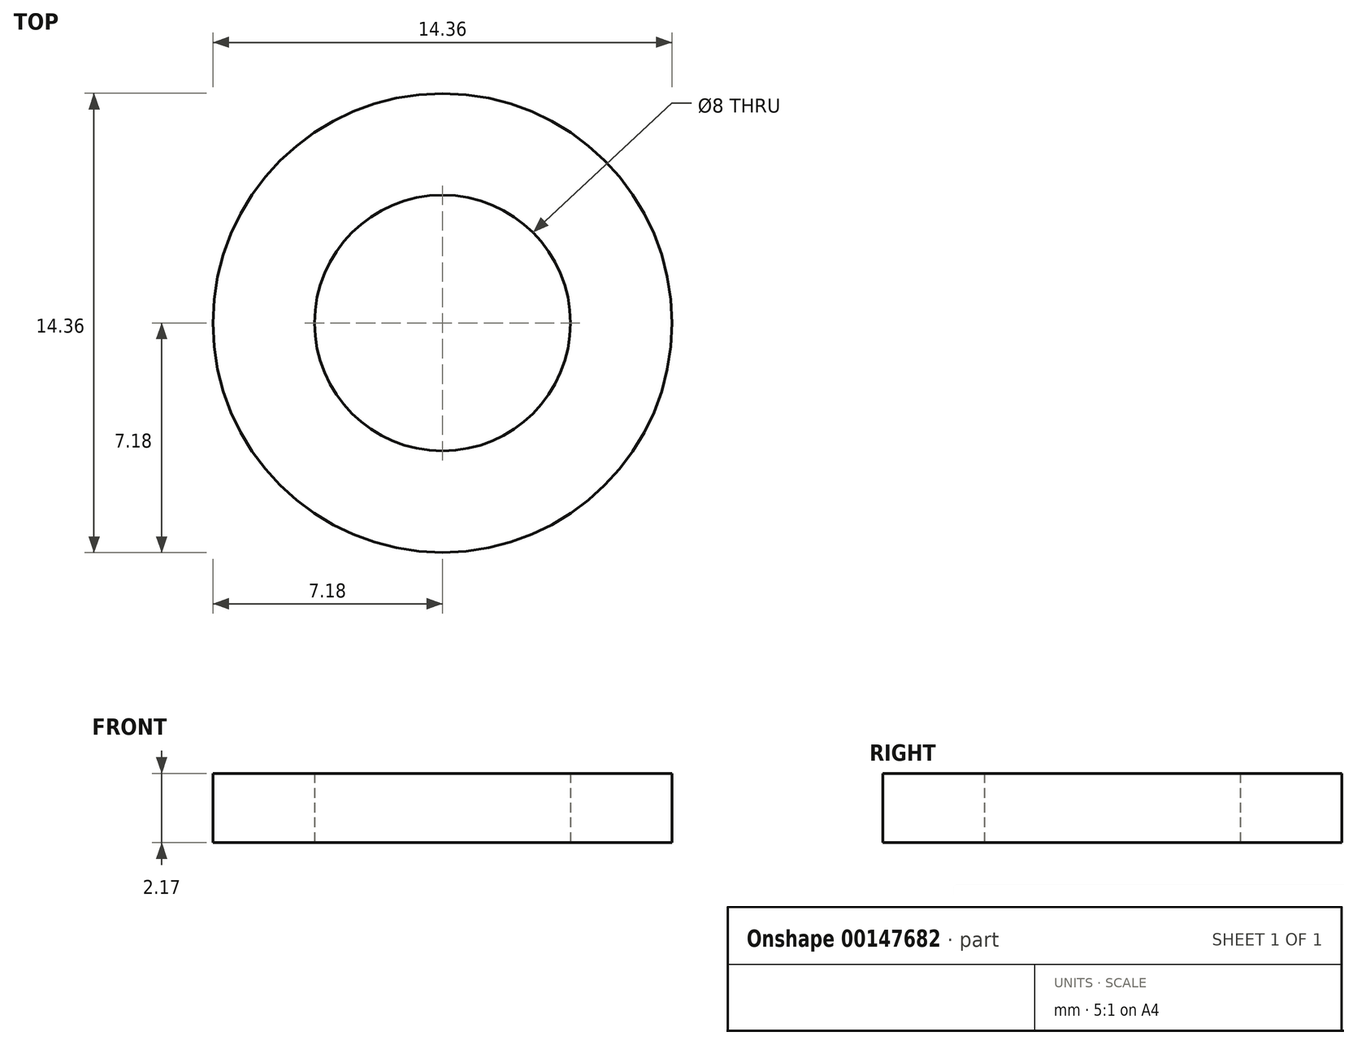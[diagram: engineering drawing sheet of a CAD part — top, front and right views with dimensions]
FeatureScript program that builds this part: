
annotation { "Feature Type Name" : "Feature", "Feature Type Description" : "" }
export const myFeature = defineFeature(function(context is Context, id is Id, definition is map)
    precondition{}
    {
        {
            var Q0;
            Q0=qCreatedBy(makeId("Top.planeOp"),FACE);
            var sketch = newSketch(context, id + "F0", { "sketchPlane" : qUnion([Q0])});
            skCircle(sketch, "E0", {"center": v(0, 0) * mm, "radius": 4 * mm});
            skCircle(sketch, "E1", {"center": v(0, 0) * mm, "radius": 7.18 * mm});
            skSolve(sketch);
        }
        {
            var Q0;
            Q0=qSketchRegion(id+"F0",true);
            extrude(context, id + "F1", {"entities" : qUnion([Q0]), "depth" : 2.17 * mm});
        }
    });
